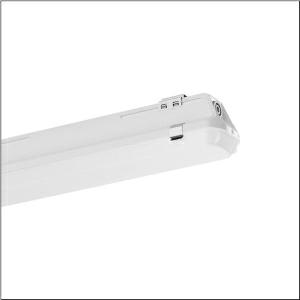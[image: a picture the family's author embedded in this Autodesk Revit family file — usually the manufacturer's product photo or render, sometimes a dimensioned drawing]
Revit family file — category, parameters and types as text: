
# Revit family: monsun_r__21_51fb12mp480b_d2d7
name_source: partatom
category: Lighting Fixtures
units: mm (PartAtom-declared; Revit-internal decimal feet)

## family parameters
Cut with Voids When Loaded = No
Host = Face
Light Source = No
Part Type = Normal
Room Calculation Point = No
Round Connector Dimension = Use Diameter
Shared = No

## types (1)
- --- (1 x LED, 8100 lm, 53.6 W, 4000K)
    Apparent Load = 54 VA
    CIE Flux Codes = 65 88 97 97 100
    Color Rendering = 80
    Color Temperature = 4000K
    Default Elevation = 1800 mm
    Description = Monsun® 21, damp-proof luminaire, chain hanger, primary light control with lens, primary optical cover: enclosure, of PMMA, light emission: direct distribution, primary light characteristic: symmetric, installation type: suspended mounting, surface-mounted, horizontal mounting, vertical mounting, LED, rated luminous flux: 8.100lm, luminous efficacy: 151lm/W, light colour: 840, colour temperature: 4000K, control gear: ECG, with terminal, 3-pole, max. 2.5mm², mains connection: 220..240V, AC, 50/60Hz, rated input power: 54W, housing, of glass-fibre reinforced polyester, uncoated, bright grey, incl. chain hanger, length: 1.590mm, width: 90mm, height: 88mm, clip for enclosure, of stainless steel (V2A), ceiling mounting element, of stainless steel (V2A), chain hanger, of stainless steel (V2A), protection rating (complete): IP66, insulation class (complete): insulation class I (protective earthing), certification: CE, ENEC, VDE, UKCA, protection symbol: D, impact resistance: IK04, permissible operating ambient temperature: -25..+35°C, standard: EN 50419, EN 60598-2-1, corresponds to IFS (International Featured Standards) requirements for safety and quality in the food industry, for indoor or canopied outdoor use, no direct snow, no direct sun, no direct rain, contact your sales advisor before using the luminaires in applications with unclear chemical exposure, large temperature fluctuations or condensation-forming humidity, LABS conformity tested according to VDMA 24364:2018-05, packaging unit: 1 piece
    Height = 89 mm
    Lamp = 1 x LED
    Lamp Light Flux = 8100 lm
    Lamp Power = 53.6 W
    Lamp count = 1
    Length = 1590 mm
    Luminous efficacy = 151 lm/W
    Manufacturer = Siteco
    ModVariant = No
    Model = 51FB12MP480B
    Mounting Place = Ceiling
    Mounting Type = Surface mounted
    Number of Poles = 1
    OnlyDefault = Yes
    Power Factor = 1
    Product Name = Monsun® 21
    Product group = damp-proof luminaire
    ProductGroupID = 301
    Protection Class = Protection class I
    Protection Degree = IP 66
    RLX_Detail_Level = 1
    RLX_Emergency_Light_Flux = 0 lm
    RLX_Emergency_Type = 0
    RLX_Emergency_Type_DB = No
    RlxData = <blob elided: 90105 chars, md5=fa001932>
    Socket = socket
    Standby Power = 0 W
    System Light Flux = 8100 lm
    System Power = 54 W
    Type Comments = factory setting: luminous flux: 100 % | (A | C | E) | 121 mA
    Type Image = l_1006717.jpg
    URL = http://relux.com
    VarID = @adj_096935
    Voltage = 0 V
    Weight = 0.00 kg
    Width = 90 mm

## geometry (parser evidence)
native form markers: Blend x4, Sweep x11
no freeform markers — native parametric forms only
